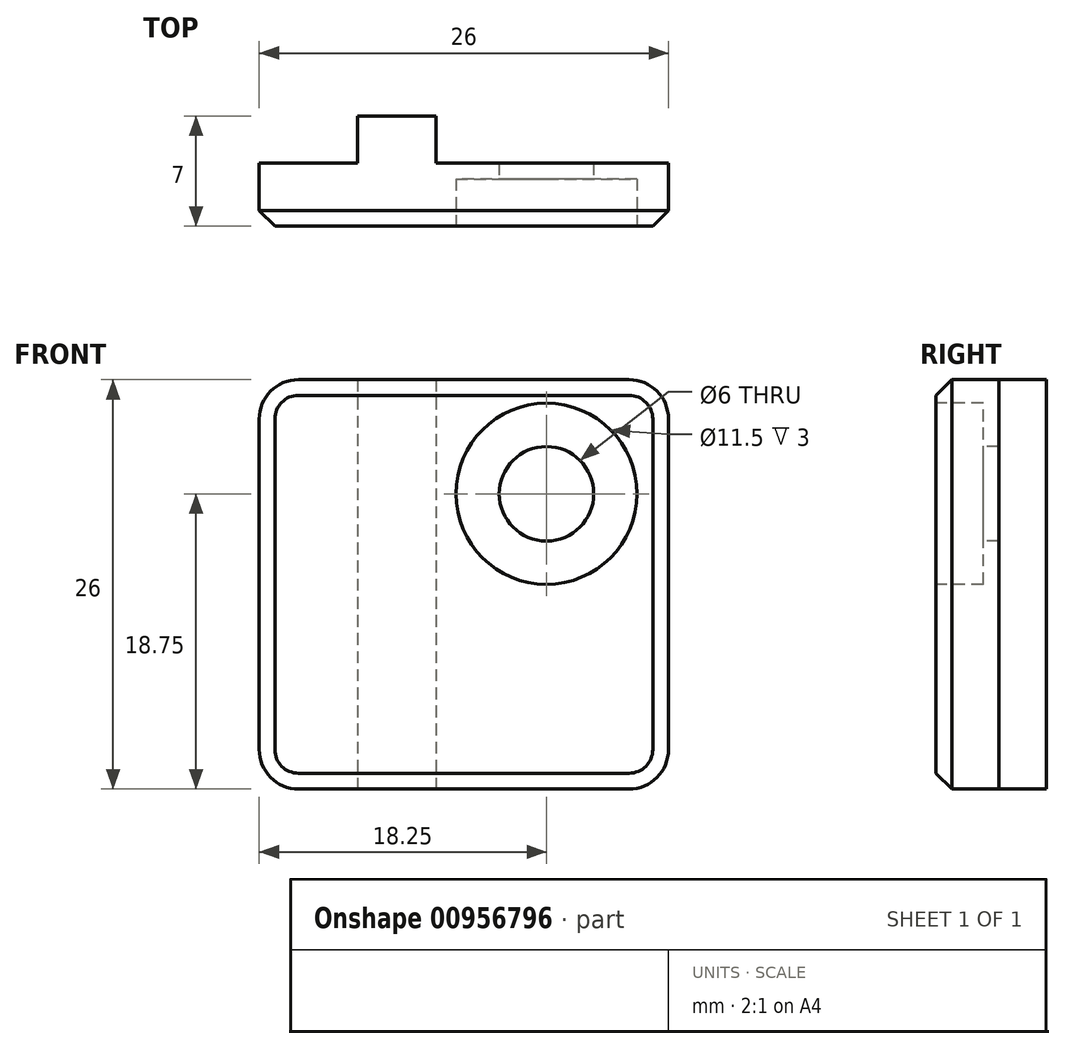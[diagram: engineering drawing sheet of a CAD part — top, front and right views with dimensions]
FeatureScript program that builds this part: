
annotation { "Feature Type Name" : "Feature", "Feature Type Description" : "" }
export const myFeature = defineFeature(function(context is Context, id is Id, definition is map)
    precondition{}
    {
        {
            var Q0;
            Q0=qCreatedBy(makeId("Front.planeOp"),FACE);
            var sketch = newSketch(context, id + "F0", { "sketchPlane" : qUnion([Q0])});
            skLineSegment(sketch, "E0.bottom", {"start": v(13, -13) * mm, "end": v(-13, -13) * mm});
            skLineSegment(sketch, "E0.top", {"start": v(13, 13) * mm, "end": v(-13, 13) * mm});
            skLineSegment(sketch, "E0.left", {"start": v(13, -13) * mm, "end": v(13, 13) * mm});
            skLineSegment(sketch, "E0.right", {"start": v(-13, -13) * mm, "end": v(-13, 13) * mm});
            skPoint(sketch, "E0.middle", {"position": v(0, 0) * mm});
            skSolve(sketch);
        }
        {
            var Q0;
            Q0 = qSketchRegion(id + "F0", true);
            extrude(context, id + "F1", {"entities" : qUnion([Q0]), "oppositeDirection" : true, "depth" : 4 * mm, "offsetDistance" : 25 * mm});
        }
        {
            var Q0;
            Q0=makeQuery(id+"F1.opExtrude","CAP_FACE",FACE,{"disambiguationData":[OSD([sQuery(id+"F0.wireOp",EDGE,"E0.bottom"),sQuery(id+"F0.wireOp",EDGE,"E0.top"),sQuery(id+"F0.wireOp",EDGE,"E0.left"),sQuery(id+"F0.wireOp",EDGE,"E0.right")])],"isStart":false});
            var sketch = newSketch(context, id + "F2", { "sketchPlane" : qUnion([Q0])});
            skLineSegment(sketch, "E1.bottom", {"start": v(6.75, 13) * mm, "end": v(1.75, 13) * mm});
            skLineSegment(sketch, "E1.top", {"start": v(6.75, -13) * mm, "end": v(1.75, -13) * mm});
            skLineSegment(sketch, "E1.left", {"start": v(6.75, 13) * mm, "end": v(6.75, -13) * mm});
            skLineSegment(sketch, "E1.right", {"start": v(1.75, 13) * mm, "end": v(1.75, -13) * mm});
            skSolve(sketch);
        }
        {
            var Q0;
            Q0 = qSketchRegion(id + "F2", true);
            extrude(context, id + "F3", {"entities" : qUnion([Q0]), "operationType" : NewBodyOperationType.ADD, "depth" : 3 * mm, "offsetDistance" : 25 * mm});
        }
        {
            var Q0;
            Q0=makeQuery(id+"F1.opExtrude","SWEPT_EDGE",EDGE,{"disambiguationData":[OSD([sQuery(id+"F0.wireOp",EDGE,"E0.top"),sQuery(id+"F0.wireOp",EDGE,"E0.right")])]});
            var Q1;
            Q1=makeQuery(id+"F1.opExtrude","SWEPT_EDGE",EDGE,{"disambiguationData":[OSD([sQuery(id+"F0.wireOp",EDGE,"E0.bottom"),sQuery(id+"F0.wireOp",EDGE,"E0.right")])]});
            var Q2;
            Q2=makeQuery(id+"F1.opExtrude","SWEPT_EDGE",EDGE,{"disambiguationData":[OSD([sQuery(id+"F0.wireOp",EDGE,"E0.top"),sQuery(id+"F0.wireOp",EDGE,"E0.left")])]});
            var Q3;
            Q3=makeQuery(id+"F1.opExtrude","SWEPT_EDGE",EDGE,{"disambiguationData":[OSD([sQuery(id+"F0.wireOp",EDGE,"E0.bottom"),sQuery(id+"F0.wireOp",EDGE,"E0.left")])]});
            fillet(context, id + "F4", {"entities" : qUnion([Q0, Q1, Q2, Q3]), "radius" : 2.5 * mm, "tangentPropagation" : true, "allowEdgeOverflow" : false});
        }
        {
            var Q0;
            Q0=makeQuery(id+"F1.opExtrude","CAP_FACE",FACE,{"disambiguationData":[OSD([sQuery(id+"F0.wireOp",EDGE,"E0.bottom"),sQuery(id+"F0.wireOp",EDGE,"E0.top"),sQuery(id+"F0.wireOp",EDGE,"E0.left"),sQuery(id+"F0.wireOp",EDGE,"E0.right")])],"isStart":true});
            var sketch = newSketch(context, id + "F5", { "sketchPlane" : qUnion([Q0])});
            skCircle(sketch, "E2", {"center": v(5.25, 5.75) * mm, "radius": 3 * mm});
            skSolve(sketch);
        }
        {
            var Q0;
            Q0 = qSketchRegion(id + "F5", true);
            extrude(context, id + "F6", {"entities" : qUnion([Q0]), "operationType" : NewBodyOperationType.REMOVE, "oppositeDirection" : true, "depth" : 25 * mm, "offsetDistance" : 25 * mm});
        }
        {
            var Q0;
            Q0=makeQuery(id+"Fgp2XBtikRpxMW6_1.opChamfer","SPLIT",FACE,{"disambiguationData":[OD(0.0)],"derivedFrom":makeQuery(id+"F1.opExtrude","CAP_FACE",FACE,{"disambiguationData":[OSD([sQuery(id+"F0.wireOp",EDGE,"E0.bottom"),sQuery(id+"F0.wireOp",EDGE,"E0.top"),sQuery(id+"F0.wireOp",EDGE,"E0.left"),sQuery(id+"F0.wireOp",EDGE,"E0.right")])],"isStart":true})});
            var sketch = newSketch(context, id + "F7", { "sketchPlane" : qUnion([Q0])});
            skCircle(sketch, "E3", {"center": v(5.25, 5.75) * mm, "radius": 5.75 * mm});
            skSolve(sketch);
        }
        {
            var Q0;
            Q0 = qSketchRegion(id + "F7", true);
            extrude(context, id + "F8", {"entities" : qUnion([Q0]), "operationType" : NewBodyOperationType.REMOVE, "oppositeDirection" : true, "depth" : 3 * mm, "offsetDistance" : 25 * mm});
        }
        {
            var Q0;
            Q0=makeQuery(id+"F1.opExtrude","CAP_EDGE",EDGE,{"disambiguationData":[OSD([sQuery(id+"F0.wireOp",EDGE,"E0.right")])],"isStart":true});
            chamfer(context, id + "F9", {"entities" : qUnion([Q0]), "width" : 1 * mm, "tangentPropagation" : true});
        }
    });
